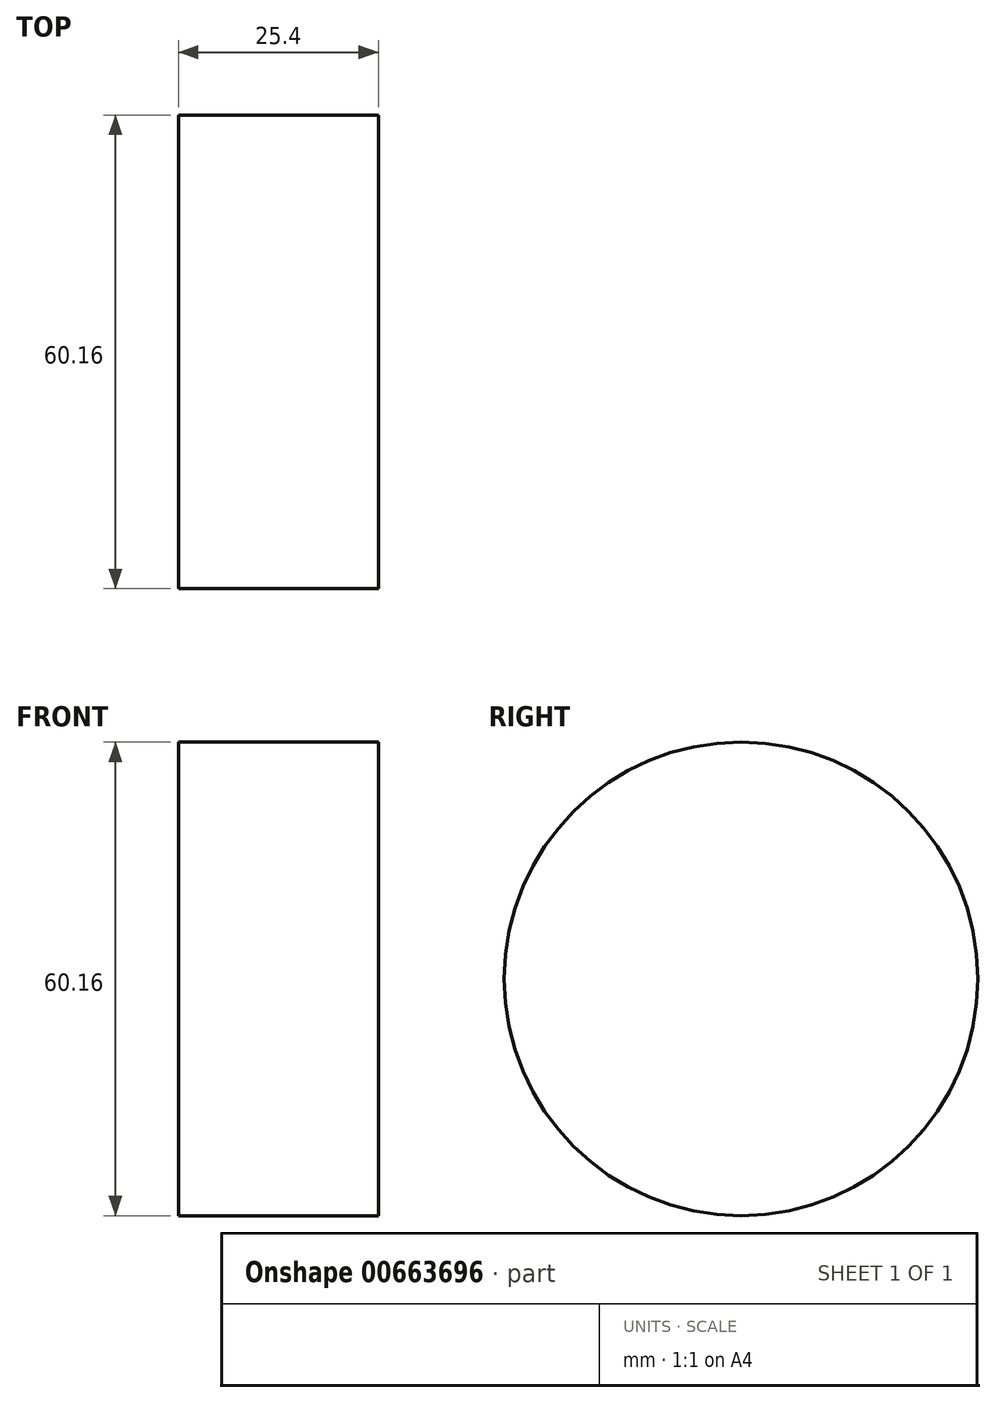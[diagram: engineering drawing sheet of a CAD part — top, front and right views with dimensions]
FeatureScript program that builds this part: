
annotation { "Feature Type Name" : "Feature", "Feature Type Description" : "" }
export const myFeature = defineFeature(function(context is Context, id is Id, definition is map)
    precondition{}
    {
        {
            var Q0;
            Q0=qCreatedBy(makeId("Right.planeOp"),FACE);
            var sketch = newSketch(context, id + "F0", { "sketchPlane" : qUnion([Q0])});
            skCircle(sketch, "E0", {"center": v(0, 0) * mm, "radius": 30.08 * mm});
            skSolve(sketch);
        }
        {
            var Q0;
            Q0 = qSketchRegion(id + "F0", true);
            extrude(context, id + "F1", {"entities" : qUnion([Q0]), "oppositeDirection" : true, "depth" : 25.4 * mm, "offsetDistance" : 25.4 * mm});
        }
    });
